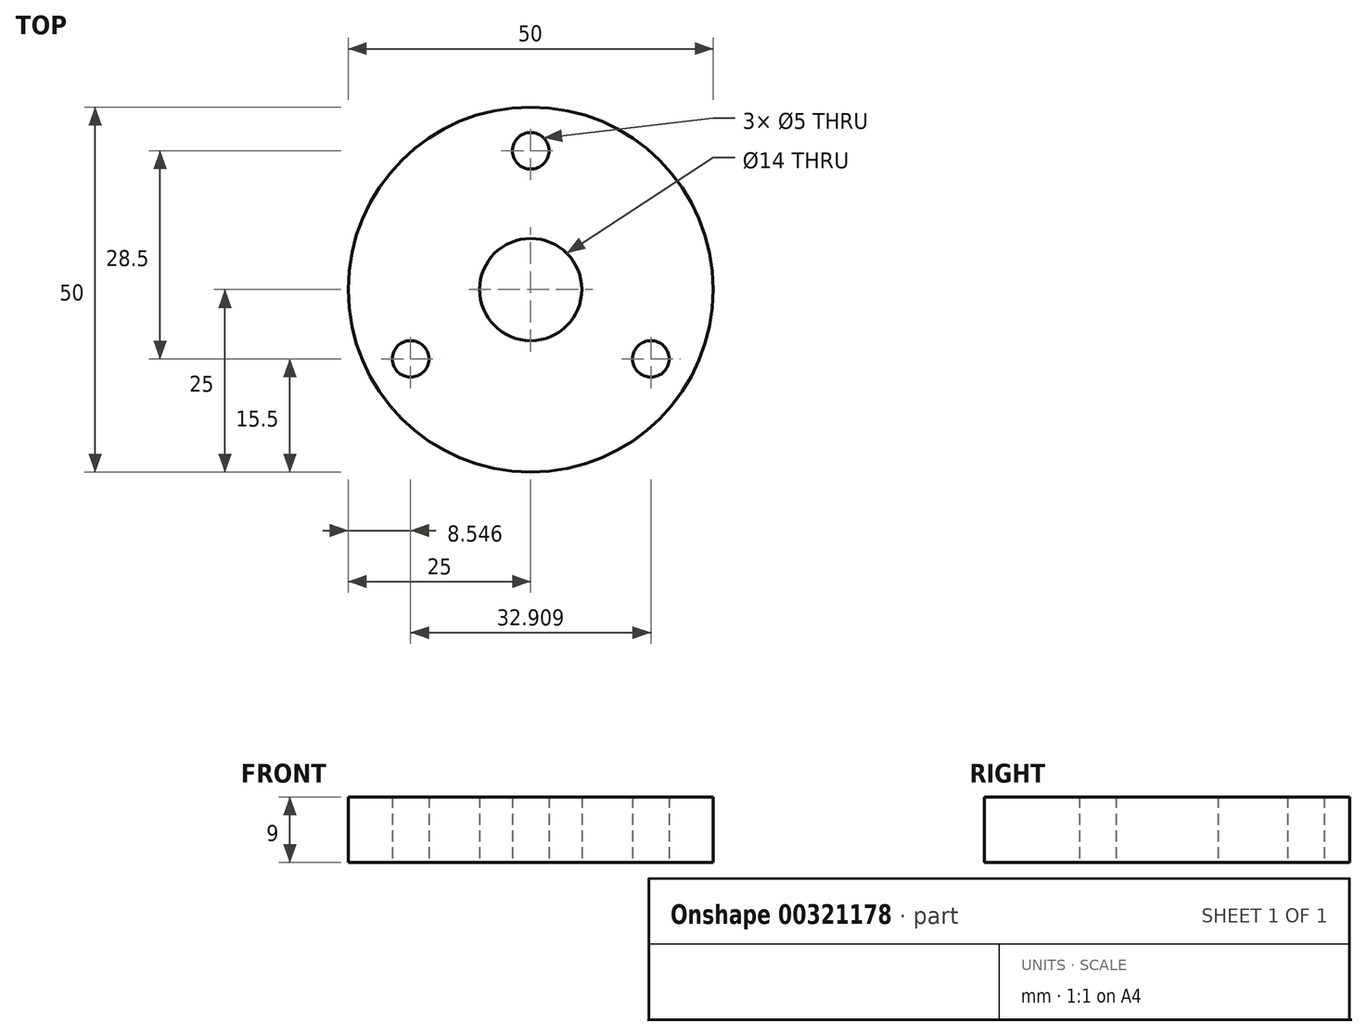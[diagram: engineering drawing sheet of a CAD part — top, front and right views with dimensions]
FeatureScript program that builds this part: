
annotation { "Feature Type Name" : "Feature", "Feature Type Description" : "" }
export const myFeature = defineFeature(function(context is Context, id is Id, definition is map)
    precondition{}
    {
        {
            var Q0;
            Q0=qCreatedBy(makeId("Top.planeOp"),FACE);
            var sketch = newSketch(context, id + "F0", { "sketchPlane" : qUnion([Q0])});
            skCircle(sketch, "E0", {"center": v(0, 0) * mm, "radius": 25 * mm});
            skCircle(sketch, "E1", {"center": v(0, 0) * mm, "radius": 7 * mm});
            skPoint(sketch, "E2", {"position": v(0, 19) * mm});
            skCircle(sketch, "E3", {"center": v(0, 19) * mm, "radius": 2.5 * mm});
            skPoint(sketch, "E4", {"position": v(-16.45, -9.5) * mm});
            skCircle(sketch, "E5", {"center": v(-16.45, -9.5) * mm, "radius": 2.5 * mm});
            skPoint(sketch, "E6", {"position": v(16.45, -9.5) * mm});
            skCircle(sketch, "E7", {"center": v(16.45, -9.5) * mm, "radius": 2.5 * mm});
            skSolve(sketch);
        }
        {
            var Q0;
            Q0=makeQuery(id+"F0.imprint","IMPRINT",FACE,{"disambiguationData":[TD([[makeQuery(id+"F0.imprint","IMPRINT",EDGE,{"derivedFrom":sQuery(id+"F0.wireOp",EDGE,"E0")}),1.0]])]});
            extrude(context, id + "F1", {"entities" : qUnion([Q0]), "depth" : 9 * mm});
        }
    });
